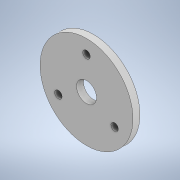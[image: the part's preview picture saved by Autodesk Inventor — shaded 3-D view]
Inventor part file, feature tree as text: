
AUTODESK INVENTOR PART (.ipt)
format: ipt  version: 2020.3 (Build 243373000, 373)  size: 114,176 bytes
history: native  units: mm
features: extrude x2, sketch x2, pattern_circular x1
ambient origin geometry x8: Origin, YZ Plane, XZ Plane, XY Plane, X Axis, Y Axis, Z Axis, Center Point
bodies: Solid1 (feature_tree)
feature tree (5):
  extrude  "Extrusion1"  Depth=8.6mm
  extrude  "Extrusion2"  Depth=10.0mm
  pattern_circular  "Circular Pattern1"  [2 undecoded]
  sketch  "Sketch1"  dims[d0=40.0mm d2=8.6mm]
  sketch  "Sketch2"  dims[d3=3.0mm d4=0.0mm d5=14.0mm d6=3.2mm d7=10.0mm d8=0.0mm d9=30.0mm d10=360.0deg d1=0.5mm]
note: 2 required parameter values undecoded (feature->parameter linkage not recoverable at this tier; creation-order binding heuristic only, values carry confidence <= 0.55)
